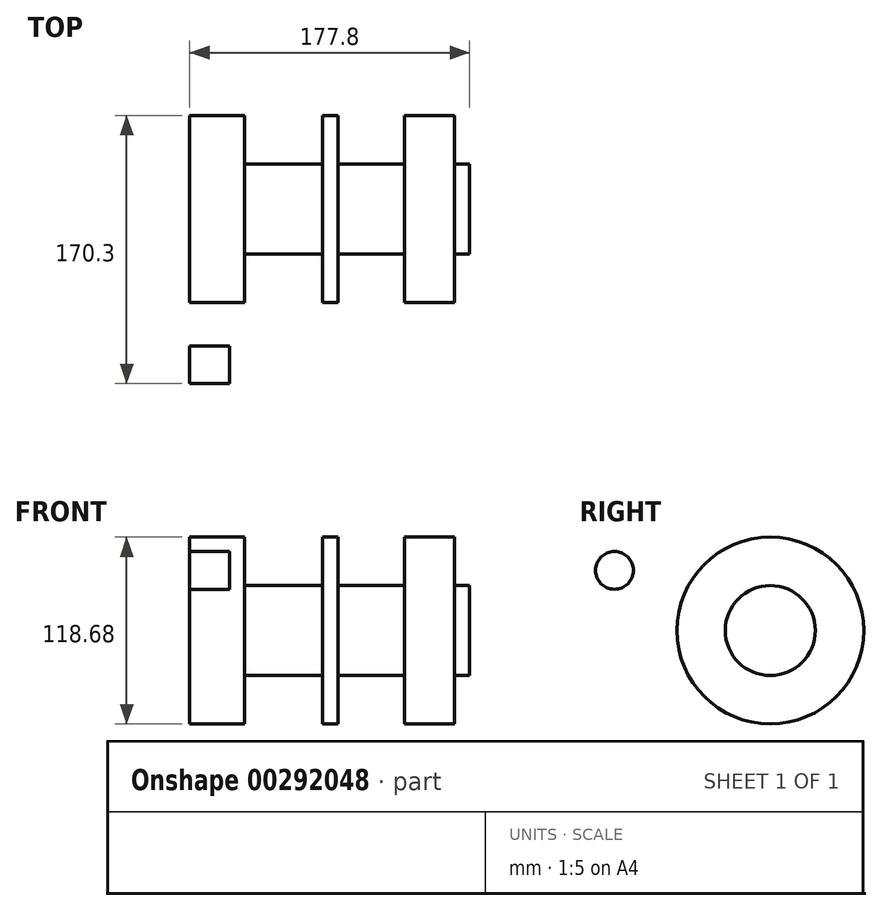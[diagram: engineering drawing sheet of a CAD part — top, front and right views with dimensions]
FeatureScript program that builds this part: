
annotation { "Feature Type Name" : "Feature", "Feature Type Description" : "" }
export const myFeature = defineFeature(function(context is Context, id is Id, definition is map)
    precondition{}
    {
        {
            var Q0;
            Q0=qCreatedBy(makeId("Right.planeOp"),FACE);
            var sketch = newSketch(context, id + "F0", { "sketchPlane" : qUnion([Q0])});
            skCircle(sketch, "E0", {"center": v(0, 0) * mm, "radius": 12.7 * mm});
            skSolve(sketch);
        }
        {
            var Q0;
            Q0 = qSketchRegion(id + "F0", true);
            extrude(context, id + "F1", {"entities" : qUnion([Q0]), "depth" : 177.8 * mm});
        }
        {
            var Q0;
            Q0=qCreatedBy(makeId("Front.planeOp"),FACE);
            var sketch = newSketch(context, id + "F2", { "sketchPlane" : qUnion([Q0])});
            skLineSegment(sketch, "E1", {"start": v(0, 12.68) * mm, "end": v(177.8, 12.68) * mm});
            skLineSegment(sketch, "E2", {"start": v(0, 0) * mm, "end": v(177.8, 0) * mm, "construction": true});
            skLineSegment(sketch, "E3", {"start": v(0, 12.68) * mm, "end": v(0, 59.34) * mm});
            skLineSegment(sketch, "E4", {"start": v(0, 59.34) * mm, "end": v(34.8, 59.34) * mm});
            skLineSegment(sketch, "E5", {"start": v(34.8, 59.34) * mm, "end": v(34.8, 28.6) * mm});
            skLineSegment(sketch, "E6", {"start": v(34.8, 28.6) * mm, "end": v(62.2, 28.6) * mm});
            skLineSegment(sketch, "E7", {"start": v(62.2, 28.6) * mm, "end": v(84.23, 28.6) * mm});
            skLineSegment(sketch, "E8", {"start": v(84.23, 28.6) * mm, "end": v(84.23, 59.34) * mm});
            skLineSegment(sketch, "E9", {"start": v(84.23, 59.34) * mm, "end": v(94.06, 59.34) * mm});
            skLineSegment(sketch, "E10", {"start": v(94.06, 59.34) * mm, "end": v(94.06, 28.6) * mm});
            skLineSegment(sketch, "E11", {"start": v(94.06, 28.6) * mm, "end": v(136.27, 28.6) * mm});
            skLineSegment(sketch, "E12", {"start": v(136.27, 28.6) * mm, "end": v(136.27, 59.34) * mm});
            skLineSegment(sketch, "E13", {"start": v(136.27, 59.34) * mm, "end": v(168.08, 59.34) * mm});
            skLineSegment(sketch, "E14", {"start": v(168.08, 59.34) * mm, "end": v(168.08, 28.6) * mm});
            skLineSegment(sketch, "E15", {"start": v(168.08, 28.6) * mm, "end": v(177.8, 28.6) * mm});
            skLineSegment(sketch, "E16", {"start": v(177.8, 28.6) * mm, "end": v(177.8, 12.68) * mm});
            skSolve(sketch);
        }
        {
            var Q0;
            Q0 = qSketchRegion(id + "F2", true);
            var Q1;
            Q1=sQuery(id+"F2.wireOp",EDGE,"E2");
            revolve(context, id + "F3", {"operationType" : NewBodyOperationType.ADD, "entities" : qUnion([Q0]), "axis" : qUnion([Q1]), "revolveType" : RevolveType.FULL});
        }
        {
            var Q0;
            Q0=qCreatedBy(makeId("Right.planeOp"),FACE);
            var sketch = newSketch(context, id + "F4", { "sketchPlane" : qUnion([Q0])});
            skCircle(sketch, "E17", {"center": v(-98.97, 38.23) * mm, "radius": 12 * mm});
            skSolve(sketch);
        }
        {
            var Q0;
            Q0=makeQuery(id+"F4.imprint","IMPRINT",FACE,{"disambiguationData":[TD([[makeQuery(id+"F4.imprint","IMPRINT",EDGE,{"derivedFrom":sQuery(id+"F4.wireOp",EDGE,"E17")}),1.0]])]});
            extrude(context, id + "F5", {"entities" : qUnion([Q0]), "depth" : 25.4 * mm});
        }
    });
